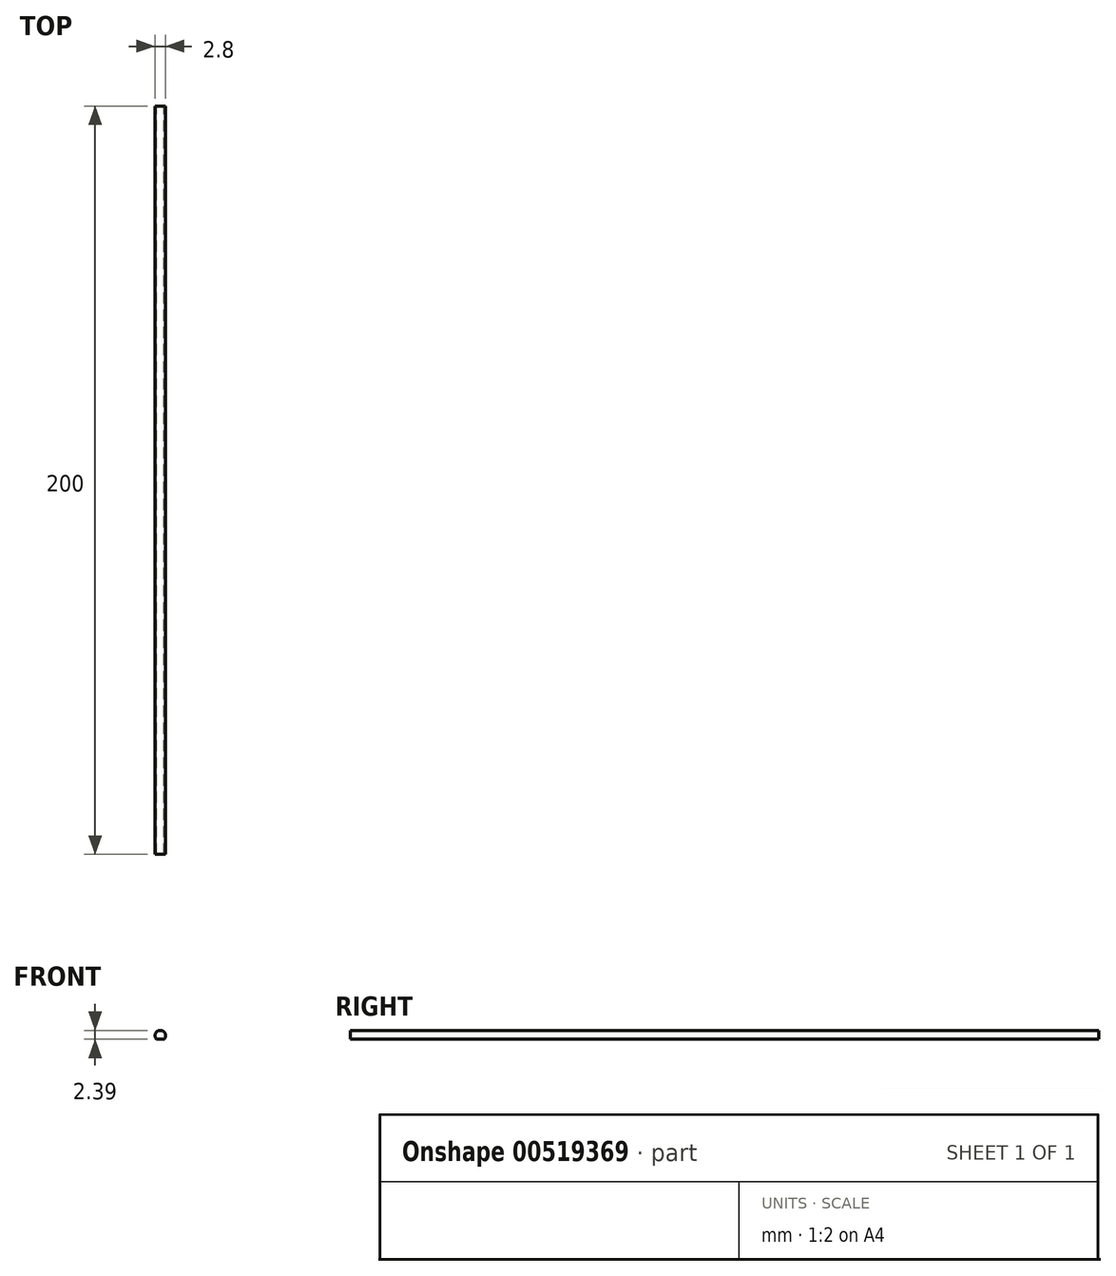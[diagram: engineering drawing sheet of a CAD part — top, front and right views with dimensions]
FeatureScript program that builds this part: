
annotation { "Feature Type Name" : "Feature", "Feature Type Description" : "" }
export const myFeature = defineFeature(function(context is Context, id is Id, definition is map)
    precondition{}
    {
        {
            var Q0;
            Q0=qCreatedBy(makeId("Front.planeOp"),FACE);
            var sketch = newSketch(context, id + "F0", { "sketchPlane" : qUnion([Q0])});
            skCircle(sketch, "E0", {"center": v(0, 0) * mm, "radius": 1.4 * mm});
            skLineSegment(sketch, "E1", {"start": v(-0.99, -0.99) * mm, "end": v(0.99, -0.99) * mm});
            skLineSegment(sketch, "E2", {"start": v(2.51, 0.53) * mm, "end": v(-0.2, -2.18) * mm, "construction": true});
            skSolve(sketch);
        }
        {
            var Q0;
            {var subQ0=sQuery(id+"F0.wireOp",EDGE,"E1");Q0=makeQuery(id+"F0.imprint","IMPRINT",FACE,{"disambiguationData":[TD([[makeQuery(id+"F0.imprint","IMPRINT",EDGE,{"derivedFrom":subQ0}),1.0]])]});}
            extrude(context, id + "F1", {"entities" : qUnion([Q0]), "depth" : 200 * mm, "offsetDistance" : 25 * mm});
        }
    });
